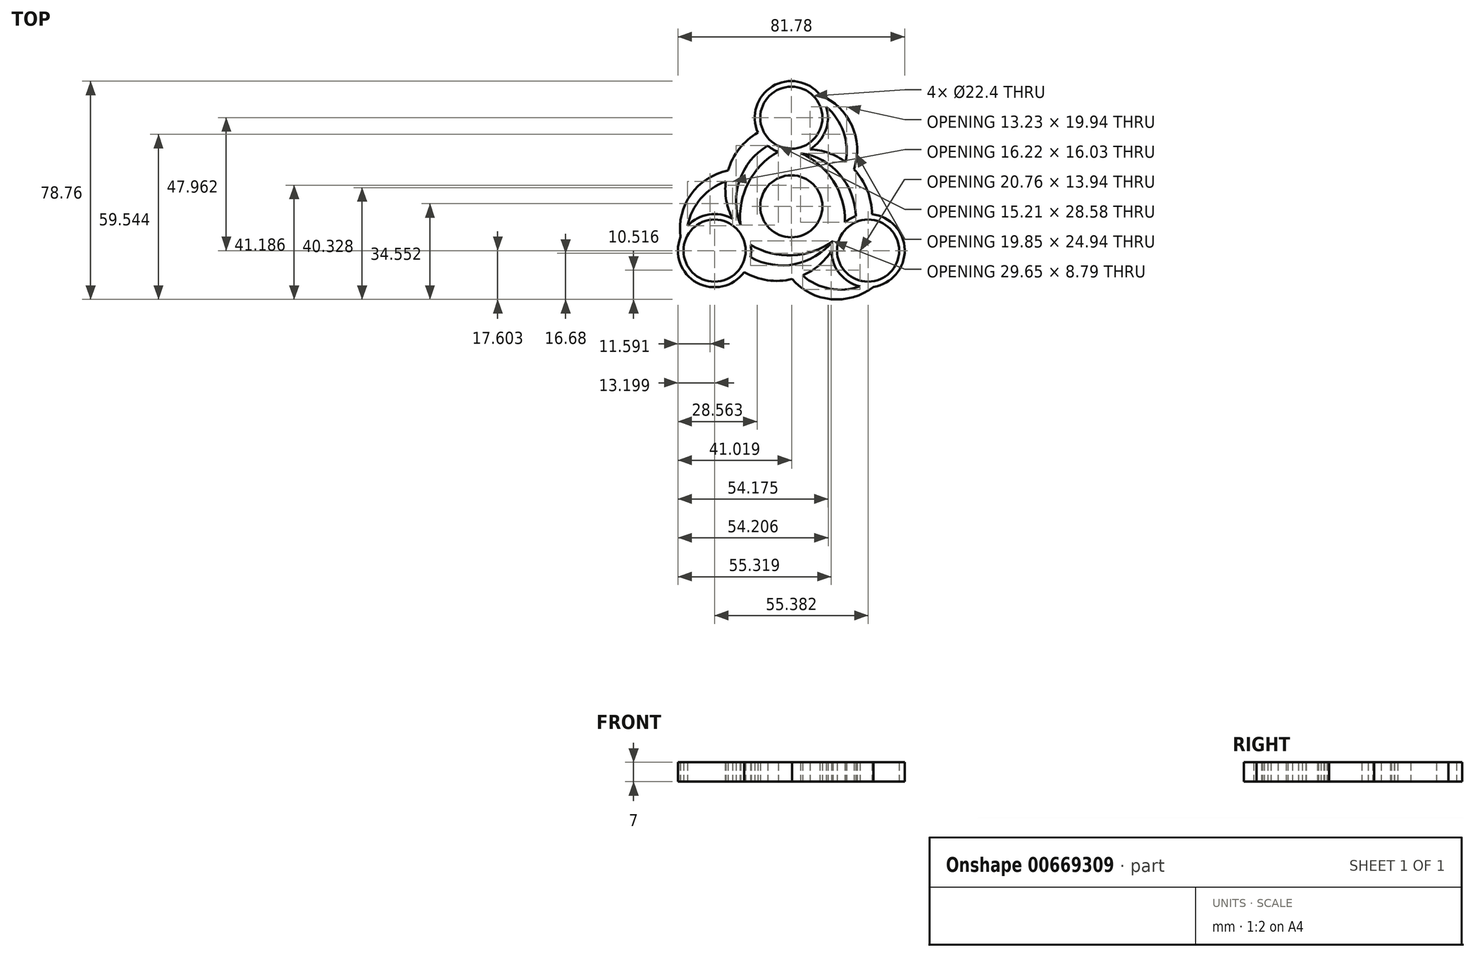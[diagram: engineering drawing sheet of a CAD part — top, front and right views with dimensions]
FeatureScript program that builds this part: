
annotation { "Feature Type Name" : "Feature", "Feature Type Description" : "" }
export const myFeature = defineFeature(function(context is Context, id is Id, definition is map)
    precondition{}
    {
        {
            var Q0;
            Q0=qCreatedBy(makeId("Top.planeOp"),FACE);
            var sketch = newSketch(context, id + "F0", { "sketchPlane" : qUnion([Q0])});
            skCircle(sketch, "E0", {"center": v(0, 0) * mm, "radius": 11.2 * mm});
            skCircle(sketch, "E1", {"center": v(0, 0) * mm, "radius": 13.2 * mm});
            skCircle(sketch, "E2", {"center": v(0, 31.97) * mm, "radius": 11.2 * mm});
            skCircle(sketch, "E3", {"center": v(0, 31.97) * mm, "radius": 13.2 * mm});
            skCircle(sketch, "E4.1.0", {"center": v(-27.7, -15.99) * mm, "radius": 11.2 * mm});
            skCircle(sketch, "E4.1.1", {"center": v(-27.7, -15.99) * mm, "radius": 13.2 * mm});
            skCircle(sketch, "E4.2.0", {"center": v(27.7, -15.99) * mm, "radius": 11.2 * mm});
            skCircle(sketch, "E4.2.1", {"center": v(27.7, -15.99) * mm, "radius": 13.2 * mm});
            skArc(sketch, "E5", {"start": v(-12.06, 26.6) * mm, "mid": v(-22.85, 12.88) * mm, "end": v(-21.2, -4.5) * mm});
            skArc(sketch, "E6.1.0", {"start": v(-17.01, -23.75) * mm, "mid": v(0.27, -26.23) * mm, "end": v(14.5, -16.1) * mm});
            skArc(sketch, "E6.2.0", {"start": v(29.07, -2.86) * mm, "mid": v(22.58, 13.35) * mm, "end": v(6.7, 20.6) * mm});
            skArc(sketch, "E7", {"start": v(-8.51, 21.89) * mm, "mid": v(-18.68, 9.4) * mm, "end": v(-18.32, -6.7) * mm});
            skArc(sketch, "E8", {"start": v(-4.72, 19.65) * mm, "mid": v(-15.5, 8.54) * mm, "end": v(-18.32, -6.7) * mm});
            skArc(sketch, "E9.1.0", {"start": v(-14.65, -13.91) * mm, "mid": v(0.36, -17.7) * mm, "end": v(14.96, -12.51) * mm});
            skArc(sketch, "E9.1.1", {"start": v(-14.7, -18.32) * mm, "mid": v(1.2, -20.88) * mm, "end": v(14.96, -12.51) * mm});
            skArc(sketch, "E9.2.0", {"start": v(19.38, -5.73) * mm, "mid": v(15.15, 9.16) * mm, "end": v(3.36, 19.2) * mm});
            skArc(sketch, "E9.2.1", {"start": v(23.21, -3.57) * mm, "mid": v(17.48, 11.47) * mm, "end": v(3.36, 19.2) * mm});
            skArc(sketch, "E10", {"start": v(19.6, 15.99) * mm, "mid": v(18.78, 26.9) * mm, "end": v(12.6, 35.92) * mm});
            skArc(sketch, "E11", {"start": v(22.58, 13.35) * mm, "mid": v(21.81, 29.2) * mm, "end": v(10.34, 40.18) * mm});
            skArc(sketch, "E12.1.0", {"start": v(-22.85, 12.88) * mm, "mid": v(-36.2, 4.29) * mm, "end": v(-39.97, -11.13) * mm});
            skArc(sketch, "E12.1.1", {"start": v(-23.64, 8.98) * mm, "mid": v(-32.68, 2.82) * mm, "end": v(-37.4, -7.05) * mm});
            skArc(sketch, "E12.2.0", {"start": v(0.27, -26.23) * mm, "mid": v(14.38, -33.5) * mm, "end": v(29.63, -29.04) * mm});
            skArc(sketch, "E12.2.1", {"start": v(4.05, -24.96) * mm, "mid": v(13.9, -29.71) * mm, "end": v(24.81, -28.87) * mm});
            skSolve(sketch);
        }
        {
            var Q0;
            Q0 = qSketchRegion(id + "F0", true);
            var Q1;
            Q1=makeQuery(id+"F0.imprint","IMPRINT",FACE,{"disambiguationData":[TD([[makeQuery(id+"F0.imprint","IMPRINT",EDGE,{"derivedFrom":sQuery(id+"F0.wireOp",EDGE,"E1")}),-1.0]])]});
            var Q2;
            Q2=makeQuery(id+"F0.imprint","IMPRINT",FACE,{"disambiguationData":[TD([[makeQuery(id+"F0.imprint","IMPRINT",EDGE,{"derivedFrom":sQuery(id+"F0.wireOp",EDGE,"E0")}),-1.0]])]});
            extrude(context, id + "F1", {"entities" : qUnion([Q0, Q1, Q2]), "depth" : 7 * mm, "offsetDistance" : 25 * mm});
        }
    });
